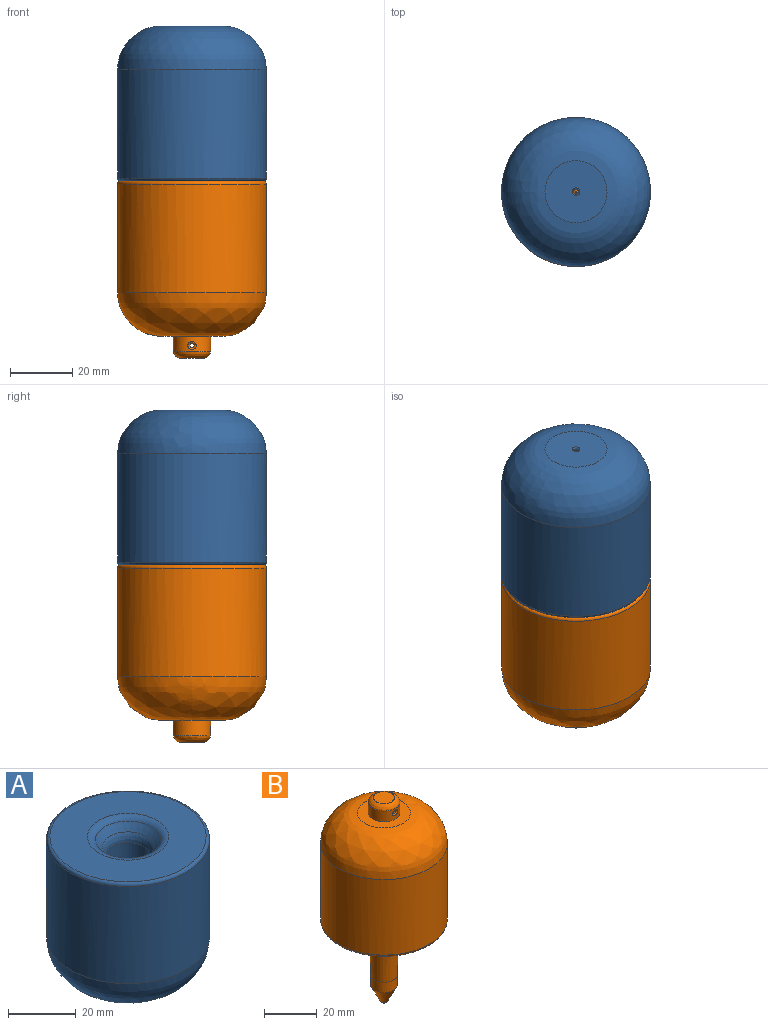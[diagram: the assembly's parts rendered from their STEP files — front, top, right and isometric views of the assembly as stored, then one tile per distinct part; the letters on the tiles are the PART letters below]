
ASSEMBLY  parts=2 mates=1
PART A: 14 faces, bbox 52x52x50 mm
  f0: cylinder r=24mm len=48mm, axis (0,0,-1), area 5277.9mm2, adj f3,f12
  f1: plane 46x46mm, normal (0,0,1), area 1213.9mm2, adj f8,f12
  f2: plane 20.01x20.01mm, normal (0,0,-1), area 309.3mm2, adj f3,f11
  f3: bspline ~48x48mm, area 2592.1mm2, adj f0,f2
  f4: cylinder r=6.5mm len=31.25mm, axis (0,0,1), area 1276.1mm2, adj f7,f13
  f5: plane 5x5mm, normal (0,0,1), area 14.7mm2, adj f10,f13
  f6: cone r=6.5mm half-angle=38.7deg, axis (0,0,1), area 173.3mm2, adj f7,f8
  f7: torus R=11.5mm, axis (0,0,-1), area 145.6mm2, adj f4,f6
  f8: torus R=11.94mm, axis (0,0,1), area 180.5mm2, adj f1,f6
  f9: cylinder r=0.75mm len=7mm, axis (0,0,-1), area 33mm2, adj f10,f11
  f10: torus R=1.25mm, axis (0,0,1), area 4.6mm2, adj f5,f9
  f11: torus R=1.25mm, axis (0,0,1), area 4.6mm2, adj f2,f9
  f12: torus R=23mm, axis (0,0,1), area 233.3mm2, adj f0,f1
  f13: torus R=2.5mm, axis (0,0,1), area 199.2mm2, adj f4,f5
PART B: 17 faces, bbox 52x52x94.8 mm
  f0: cylinder r=24mm len=48mm, axis (0,0,-1), area 5277.9mm2, adj f3,f9
  f1: plane 20.01x20.01mm, normal (0,0,1), area 201.1mm2, adj f3,f10
  f2: plane 46.01x46.01mm, normal (0,0,-1), area 1370.2mm2, adj f9,f16
  f3: bspline ~48x48mm, area 2592.1mm2, adj f0,f1
  f4: cone r=5.75mm half-angle=1.7deg, axis (0,0,1), area 705.9mm2, adj f5,f16
  f5: cylinder r=5mm len=10mm, axis (0,0,1), area 149.2mm2, adj f4,f7
  f6: plane 0.15x0.15mm, normal (0,0,-1), area 0mm2, adj f8
  f7: cone r=1mm half-angle=26.6deg, axis (0,0,1), area 161.6mm2, adj f5,f8
  f8: torus R=0.07mm, axis (0,0,-1), area 8.6mm2, adj f6,f7
  f9: torus R=23mm, axis (0,0,1), area 233.3mm2, adj f0,f2
  f10: cylinder r=6mm len=12mm, axis (0,0,-1), area 177.7mm2, adj f1,f12,f14,f15
  f11: plane 8x8mm, normal (0,0,1), area 50.3mm2, adj f12
  f12: bspline ~12x12mm, area 98.8mm2, adj f10,f11
  f13: cylinder r=0.75mm len=10.98mm, axis (0,-1,0), area 51.8mm2, adj f14,f15
  f14: bspline ~2.73x2.5mm, area 5.1mm2, adj f10,f13
  f15: bspline ~2.73x2.5mm, area 5.1mm2, adj f10,f13
  f16: bspline ~19.26x19.26mm, area 274.4mm2, adj f2,f4
PLACE A rot(axis=(0,1,0),180deg) t=(-14.22,-11.14,124.55)mm
PLACE B rot(axis=(0,1,0),180deg) t=(-14.22,-11.14,74.55)mm fixed
MATE slider A.f0 <-> B.f0  axis (0,0,-1) through (-14.22,-11.14,74.55)mm
